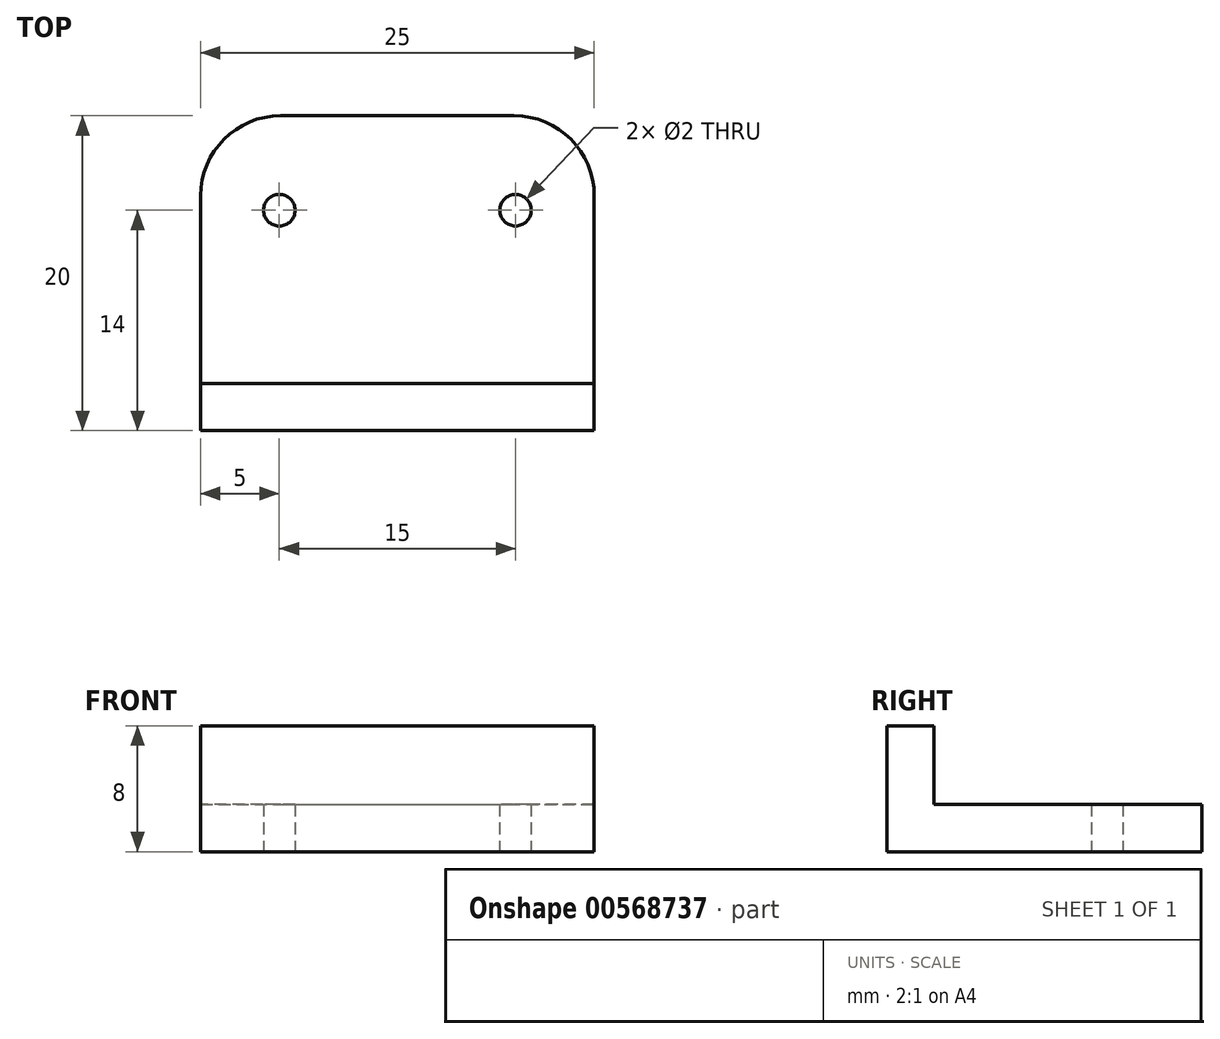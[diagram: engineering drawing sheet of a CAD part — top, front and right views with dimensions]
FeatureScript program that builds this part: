
annotation { "Feature Type Name" : "Feature", "Feature Type Description" : "" }
export const myFeature = defineFeature(function(context is Context, id is Id, definition is map)
    precondition{}
    {
        {
            var Q0;
            Q0=qCreatedBy(makeId("Top.planeOp"),FACE);
            var sketch = newSketch(context, id + "F0", { "sketchPlane" : qUnion([Q0])});
            skLineSegment(sketch, "E0", {"start": v(0, 0) * mm, "end": v(25, 0) * mm});
            skLineSegment(sketch, "E1", {"start": v(25, 0) * mm, "end": v(25, 14.92) * mm});
            skLineSegment(sketch, "E2", {"start": v(0, 0) * mm, "end": v(0, 14.92) * mm});
            skLineSegment(sketch, "E3", {"start": v(5.08, 20) * mm, "end": v(19.92, 20) * mm});
            skPoint(sketch, "E4.visualSharp", {"position": v(0, 20) * mm});
            skArc(sketch, "E4.filletArc", {"start": v(5.08, 20) * mm, "mid": v(1.49, 18.51) * mm, "end": v(0, 14.92) * mm});
            skPoint(sketch, "E5.visualSharp", {"position": v(25, 20) * mm});
            skArc(sketch, "E5.filletArc", {"start": v(25, 14.92) * mm, "mid": v(23.51, 18.51) * mm, "end": v(19.92, 20) * mm});
            skCircle(sketch, "E6", {"center": v(5, 14) * mm, "radius": 1 * mm});
            skCircle(sketch, "E7", {"center": v(20, 14) * mm, "radius": 1 * mm});
            skSolve(sketch);
        }
        {
            var Q0;
            Q0 = qSketchRegion(id + "F0", true);
            extrude(context, id + "F1", {"entities" : qUnion([Q0]), "depth" : 3 * mm, "offsetDistance" : 25.4 * mm});
        }
        {
            var Q0;
            Q0=makeQuery(id+"F1.opExtrude","CAP_FACE",FACE,{"disambiguationData":[OSD([sQuery(id+"F0.wireOp",EDGE,"E0"),sQuery(id+"F0.wireOp",EDGE,"E1"),sQuery(id+"F0.wireOp",EDGE,"E2"),sQuery(id+"F0.wireOp",EDGE,"E3"),sQuery(id+"F0.wireOp",EDGE,"E4.filletArc"),sQuery(id+"F0.wireOp",EDGE,"E5.filletArc"),sQuery(id+"F0.wireOp",EDGE,"E6"),sQuery(id+"F0.wireOp",EDGE,"E7")])],"isStart":false});
            var sketch = newSketch(context, id + "F2", { "sketchPlane" : qUnion([Q0])});
            skLineSegment(sketch, "E8", {"start": v(0, 0) * mm, "end": v(0, 3) * mm});
            skLineSegment(sketch, "E9", {"start": v(0, 3) * mm, "end": v(25, 3) * mm});
            skLineSegment(sketch, "E10", {"start": v(25, 3) * mm, "end": v(25, 0) * mm});
            skLineSegment(sketch, "E11", {"start": v(25, 0) * mm, "end": v(0, 0) * mm});
            skSolve(sketch);
        }
        {
            var Q0;
            Q0 = qSketchRegion(id + "F2", true);
            extrude(context, id + "F3", {"entities" : qUnion([Q0]), "operationType" : NewBodyOperationType.ADD, "depth" : 5 * mm, "offsetDistance" : 25.4 * mm});
        }
    });
